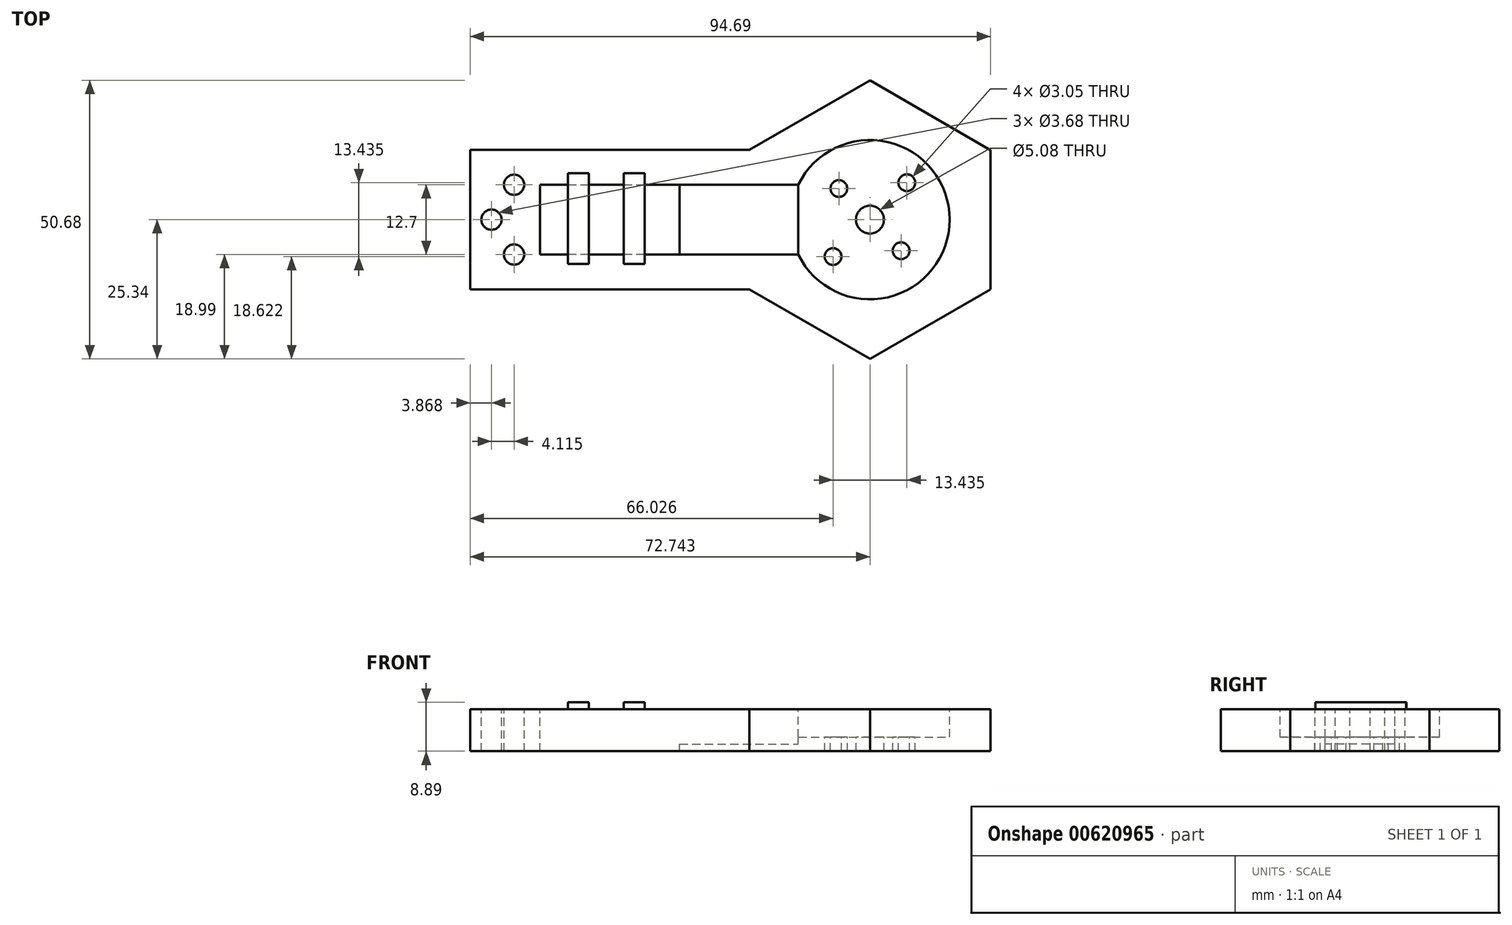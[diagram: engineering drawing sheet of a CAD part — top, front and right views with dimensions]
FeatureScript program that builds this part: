
annotation { "Feature Type Name" : "Feature", "Feature Type Description" : "" }
export const myFeature = defineFeature(function(context is Context, id is Id, definition is map)
    precondition{}
    {
        {
            var Q0;
            Q0=qCreatedBy(makeId("Top.planeOp"),FACE);
            var sketch = newSketch(context, id + "F0", { "sketchPlane" : qUnion([Q0])});
            skLineSegment(sketch, "E0.bottom", {"start": v(50.8, -12.7) * mm, "end": v(0, -12.7) * mm});
            skLineSegment(sketch, "E0.top", {"start": v(50.8, 12.7) * mm, "end": v(0, 12.7) * mm});
            skLineSegment(sketch, "E0.left", {"start": v(50.8, -12.7) * mm, "end": v(50.8, 12.7) * mm});
            skPoint(sketch, "E0.middle", {"position": v(0, 0) * mm});
            skLineSegment(sketch, "E1", {"start": v(0, 12.7) * mm, "end": v(0, -12.7) * mm});
            skPoint(sketch, "E2.orphan", {"position": v(-50.8, 12.7) * mm});
            skPoint(sketch, "E3.orphan", {"position": v(-50.8, -12.7) * mm});
            skSolve(sketch);
        }
        {
            var Q0;
            Q0=makeQuery(id+"F0.imprint","IMPRINT",FACE,{"disambiguationData":[TD([[makeQuery(id+"F0.imprint","IMPRINT",EDGE,{"derivedFrom":sQuery(id+"F0.wireOp",EDGE,"E0.bottom")}),-1.0]])]});
            extrude(context, id + "F1", {"entities" : qUnion([Q0]), "depth" : 7.62 * mm, "offsetDistance" : 25.4 * mm});
        }
        {
            var Q0;
            Q0=qCreatedBy(makeId("Top.planeOp"),FACE);
            var sketch = newSketch(context, id + "F2", { "sketchPlane" : qUnion([Q0])});
            skCircle(sketch, "E4.cCircle", {"center": v(72.74, 0) * mm, "radius": 21.95 * mm, "construction": true});
            skLineSegment(sketch, "E4.0", {"start": v(94.7, 12.67) * mm, "end": v(94.7, -12.67) * mm});
            skLineSegment(sketch, "E4.1", {"start": v(94.7, -12.67) * mm, "end": v(72.74, -25.34) * mm});
            skLineSegment(sketch, "E4.2", {"start": v(72.74, -25.34) * mm, "end": v(50.8, -12.67) * mm});
            skLineSegment(sketch, "E4.3", {"start": v(50.8, -12.67) * mm, "end": v(50.8, 12.67) * mm});
            skLineSegment(sketch, "E4.4", {"start": v(50.8, 12.67) * mm, "end": v(72.74, 25.34) * mm});
            skLineSegment(sketch, "E4.5", {"start": v(72.74, 25.34) * mm, "end": v(94.7, 12.67) * mm});
            skPoint(sketch, "E4.0.midPoint", {"position": v(94.7, 0) * mm});
            skSolve(sketch);
        }
        {
            var Q0;
            Q0=makeQuery(id+"F2.imprint","IMPRINT",FACE,{"disambiguationData":[TD([[makeQuery(id+"F2.imprint","IMPRINT",EDGE,{"derivedFrom":sQuery(id+"F2.wireOp",EDGE,"E4.0")}),-1.0]])]});
            extrude(context, id + "F3", {"entities" : qUnion([Q0]), "depth" : 7.62 * mm, "offsetDistance" : 25.4 * mm});
        }
        {
            var Q0;
            Q0=makeQuery(id+"F1.opExtrude","CAP_FACE",FACE,{"disambiguationData":[OSD([sQuery(id+"F0.wireOp",EDGE,"E0.bottom"),sQuery(id+"F0.wireOp",EDGE,"E0.top"),sQuery(id+"F0.wireOp",EDGE,"E0.left"),sQuery(id+"F0.wireOp",EDGE,"E0.right")])],"isStart":false});
            var sketch = newSketch(context, id + "F4", { "sketchPlane" : qUnion([Q0])});
            skLineSegment(sketch, "E5", {"start": v(12.7, 6.35) * mm, "end": v(38.1, 6.35) * mm});
            skLineSegment(sketch, "E6", {"start": v(38.1, 6.35) * mm, "end": v(38.1, -6.35) * mm});
            skLineSegment(sketch, "E7", {"start": v(38.1, -6.35) * mm, "end": v(12.7, -6.35) * mm});
            skLineSegment(sketch, "E8", {"start": v(12.7, -6.35) * mm, "end": v(12.7, 6.35) * mm});
            skSolve(sketch);
        }
        {
            var Q0;
            Q0=makeQuery(id+"F4.imprint","IMPRINT",FACE,{"disambiguationData":[TD([[makeQuery(id+"F4.imprint","IMPRINT",EDGE,{"derivedFrom":sQuery(id+"F4.wireOp",EDGE,"E5")}),-1.0]])]});
            extrude(context, id + "F5", {"entities" : qUnion([Q0]), "operationType" : NewBodyOperationType.REMOVE, "endBound" : BoundingType.THROUGH_ALL, "oppositeDirection" : true, "depth" : 25.4 * mm, "offsetDistance" : 25.4 * mm});
        }
        {
            var Q0;
            Q0=makeQuery(id+"F3.opExtrude","CAP_FACE",FACE,{"disambiguationData":[OSD([sQuery(id+"F2.wireOp",EDGE,"E4.0"),sQuery(id+"F2.wireOp",EDGE,"E4.1"),sQuery(id+"F2.wireOp",EDGE,"E4.2"),sQuery(id+"F2.wireOp",EDGE,"E4.3"),sQuery(id+"F2.wireOp",EDGE,"E4.4"),sQuery(id+"F2.wireOp",EDGE,"E4.5")])],"isStart":false});
            var sketch = newSketch(context, id + "F6", { "sketchPlane" : qUnion([Q0])});
            skCircle(sketch, "E9", {"center": v(72.74, 0) * mm, "radius": 14.5 * mm});
            skSolve(sketch);
        }
        {
            var Q0;
            Q0=qSketchRegion(id+"F6",true);
            extrude(context, id + "F7", {"entities" : qUnion([Q0]), "operationType" : NewBodyOperationType.REMOVE, "oppositeDirection" : true, "depth" : 5.08 * mm, "offsetDistance" : 25.4 * mm});
        }
        {
            var Q0;
            Q0=makeQuery(id+"F7.boolean.opBoolean","COPY",FACE,{"derivedFrom":makeQuery(id+"F7.opExtrude","CAP_FACE",FACE,{"disambiguationData":[OSD([sQuery(id+"F6.wireOp",EDGE,"E9")])],"isStart":false})});
            var sketch = newSketch(context, id + "F8", { "sketchPlane" : qUnion([Q0])});
            skLineSegment(sketch, "E10", {"start": v(72.74, 0) * mm, "end": v(79.46, 6.72) * mm});
            skSolve(sketch);
        }
        {
            var Q0;
            Q0=makeQuery(id+"F8.imprint","IMPRINT",FACE,{"disambiguationData":[TD([[makeQuery(id+"F8.imprint","IMPRINT",EDGE,{"derivedFrom":makeQuery(id+"F7.boolean.opBoolean","COPY",EDGE,{"derivedFrom":makeQuery(id+"F7.opExtrude","CAP_EDGE",EDGE,{"disambiguationData":[OSD([sQuery(id+"F6.wireOp",EDGE,"E9")])],"isStart":false})})}),1.0]])]});
            var sketch = newSketch(context, id + "F9", { "sketchPlane" : qUnion([Q0])});
            skCircle(sketch, "E11", {"center": v(67.09, 5.66) * mm, "radius": 1.52 * mm});
            skSolve(sketch);
        }
        {
            var Q0;
            Q0=makeQuery(id+"F8.imprint","IMPRINT",FACE,{"disambiguationData":[TD([[makeQuery(id+"F8.imprint","IMPRINT",EDGE,{"derivedFrom":makeQuery(id+"F7.boolean.opBoolean","COPY",EDGE,{"derivedFrom":makeQuery(id+"F7.opExtrude","CAP_EDGE",EDGE,{"disambiguationData":[OSD([sQuery(id+"F6.wireOp",EDGE,"E9")])],"isStart":false})})}),1.0]])]});
            var sketch = newSketch(context, id + "F10", { "sketchPlane" : qUnion([Q0])});
            skCircle(sketch, "E12", {"center": v(79.46, 6.72) * mm, "radius": 1.52 * mm});
            skSolve(sketch);
        }
        {
            var Q0;
            Q0=makeQuery(id+"F8.imprint","IMPRINT",FACE,{"disambiguationData":[TD([[makeQuery(id+"F8.imprint","IMPRINT",EDGE,{"derivedFrom":makeQuery(id+"F7.boolean.opBoolean","COPY",EDGE,{"derivedFrom":makeQuery(id+"F7.opExtrude","CAP_EDGE",EDGE,{"disambiguationData":[OSD([sQuery(id+"F6.wireOp",EDGE,"E9")])],"isStart":false})})}),1.0]])]});
            var sketch = newSketch(context, id + "F11", { "sketchPlane" : qUnion([Q0])});
            skCircle(sketch, "E13", {"center": v(78.4, -5.66) * mm, "radius": 1.52 * mm});
            skSolve(sketch);
        }
        {
            var Q0;
            Q0=makeQuery(id+"F8.imprint","IMPRINT",FACE,{"disambiguationData":[TD([[makeQuery(id+"F8.imprint","IMPRINT",EDGE,{"derivedFrom":makeQuery(id+"F7.boolean.opBoolean","COPY",EDGE,{"derivedFrom":makeQuery(id+"F7.opExtrude","CAP_EDGE",EDGE,{"disambiguationData":[OSD([sQuery(id+"F6.wireOp",EDGE,"E9")])],"isStart":false})})}),1.0]])]});
            var sketch = newSketch(context, id + "F12", { "sketchPlane" : qUnion([Q0])});
            skCircle(sketch, "E14", {"center": v(66.03, -6.72) * mm, "radius": 1.52 * mm});
            skSolve(sketch);
        }
        {
            var Q0;
            Q0=qSketchRegion(id+"F9",true);
            extrude(context, id + "F13", {"entities" : qUnion([Q0]), "operationType" : NewBodyOperationType.REMOVE, "endBound" : BoundingType.THROUGH_ALL, "oppositeDirection" : true, "depth" : 25.4 * mm, "offsetDistance" : 25.4 * mm});
        }
        {
            var Q0;
            Q0=qSketchRegion(id+"F10",true);
            extrude(context, id + "F14", {"entities" : qUnion([Q0]), "operationType" : NewBodyOperationType.REMOVE, "endBound" : BoundingType.THROUGH_ALL, "oppositeDirection" : true, "depth" : 25.4 * mm, "offsetDistance" : 25.4 * mm});
        }
        {
            var Q0;
            Q0=qSketchRegion(id+"F11",true);
            extrude(context, id + "F15", {"entities" : qUnion([Q0]), "operationType" : NewBodyOperationType.REMOVE, "endBound" : BoundingType.THROUGH_ALL, "oppositeDirection" : true, "depth" : 25.4 * mm, "offsetDistance" : 25.4 * mm});
        }
        {
            var Q0;
            Q0=qSketchRegion(id+"F12",true);
            extrude(context, id + "F16", {"entities" : qUnion([Q0]), "operationType" : NewBodyOperationType.REMOVE, "endBound" : BoundingType.THROUGH_ALL, "oppositeDirection" : true, "depth" : 25.4 * mm, "offsetDistance" : 25.4 * mm});
        }
        {
            var Q0;
            Q0=makeQuery(id+"F1.opExtrude","CAP_FACE",FACE,{"disambiguationData":[OSD([sQuery(id+"F0.wireOp",EDGE,"E0.bottom"),sQuery(id+"F0.wireOp",EDGE,"E0.top"),sQuery(id+"F0.wireOp",EDGE,"E0.left"),sQuery(id+"F0.wireOp",EDGE,"E0.right")])],"isStart":false});
            var sketch = newSketch(context, id + "F17", { "sketchPlane" : qUnion([Q0])});
            skLineSegment(sketch, "E15.bottom", {"start": v(17.78, -8.04) * mm, "end": v(21.59, -8.04) * mm});
            skLineSegment(sketch, "E15.top", {"start": v(17.78, 8.47) * mm, "end": v(21.59, 8.47) * mm});
            skLineSegment(sketch, "E15.left", {"start": v(17.78, -8.04) * mm, "end": v(17.78, 8.47) * mm});
            skLineSegment(sketch, "E15.right", {"start": v(21.59, -8.04) * mm, "end": v(21.59, 8.47) * mm});
            skLineSegment(sketch, "E16.bottom", {"start": v(27.94, -8.08) * mm, "end": v(31.75, -8.08) * mm});
            skLineSegment(sketch, "E16.top", {"start": v(27.94, 8.43) * mm, "end": v(31.75, 8.43) * mm});
            skLineSegment(sketch, "E16.left", {"start": v(27.94, -8.08) * mm, "end": v(27.94, 8.43) * mm});
            skLineSegment(sketch, "E16.right", {"start": v(31.75, -8.08) * mm, "end": v(31.75, 8.43) * mm});
            skSolve(sketch);
        }
        {
            var Q0;
            Q0=qSketchRegion(id+"F17",true);
            extrude(context, id + "F18", {"entities" : qUnion([Q0]), "operationType" : NewBodyOperationType.ADD, "depth" : 1.27 * mm, "offsetDistance" : 25.4 * mm});
        }
        {
            var Q0;
            Q0=makeQuery(id+"F1.opExtrude","CAP_FACE",FACE,{"disambiguationData":[OSD([sQuery(id+"F0.wireOp",EDGE,"E0.bottom"),sQuery(id+"F0.wireOp",EDGE,"E0.top"),sQuery(id+"F0.wireOp",EDGE,"E0.left"),sQuery(id+"F0.wireOp",EDGE,"E0.right")])],"isStart":false});
            var sketch = newSketch(context, id + "F19", { "sketchPlane" : qUnion([Q0])});
            skCircle(sketch, "E17", {"center": v(7.98, -6.35) * mm, "radius": 1.84 * mm});
            skCircle(sketch, "E18", {"center": v(7.98, 6.35) * mm, "radius": 1.84 * mm});
            skCircle(sketch, "E19", {"center": v(3.87, 0) * mm, "radius": 1.84 * mm});
            skSolve(sketch);
        }
        {
            var Q0;
            Q0=qSketchRegion(id+"F19",true);
            extrude(context, id + "F20", {"entities" : qUnion([Q0]), "operationType" : NewBodyOperationType.REMOVE, "endBound" : BoundingType.THROUGH_ALL, "oppositeDirection" : true, "depth" : 25.4 * mm, "offsetDistance" : 25.4 * mm});
        }
        {
            var Q0;
            Q0=makeQuery(id+"F1.opExtrude","SWEPT_BODY",BODY,{"disambiguationData":[OSD([sQuery(id+"F0.wireOp",EDGE,"E0.bottom"),sQuery(id+"F0.wireOp",EDGE,"E0.top"),sQuery(id+"F0.wireOp",EDGE,"E0.left"),sQuery(id+"F0.wireOp",EDGE,"E1")])]});
            var Q1;
            Q1=makeQuery(id+"F3.opExtrude","SWEPT_BODY",BODY,{"disambiguationData":[OSD([sQuery(id+"F2.wireOp",EDGE,"E4.0"),sQuery(id+"F2.wireOp",EDGE,"E4.1"),sQuery(id+"F2.wireOp",EDGE,"E4.2"),sQuery(id+"F2.wireOp",EDGE,"E4.3"),sQuery(id+"F2.wireOp",EDGE,"E4.4"),sQuery(id+"F2.wireOp",EDGE,"E4.5")])]});
            booleanBodies(context, id + "F21", {"operationType" : BooleanOperationType.UNION, "tools" : qUnion([Q0, Q1])});
        }
        {
            var Q0;
            Q0=makeQuery(id+"F21.opBoolean","MERGE",FACE,{"derivedFrom":[makeQuery(id+"F3.opExtrude","CAP_FACE",FACE,{"disambiguationData":[OSD([sQuery(id+"F2.wireOp",EDGE,"E4.0"),sQuery(id+"F2.wireOp",EDGE,"E4.1"),sQuery(id+"F2.wireOp",EDGE,"E4.2"),sQuery(id+"F2.wireOp",EDGE,"E4.3"),sQuery(id+"F2.wireOp",EDGE,"E4.4"),sQuery(id+"F2.wireOp",EDGE,"E4.5")])],"isStart":false}),makeQuery(id+"F1.opExtrude","CAP_FACE",FACE,{"disambiguationData":[OSD([sQuery(id+"F0.wireOp",EDGE,"E0.bottom"),sQuery(id+"F0.wireOp",EDGE,"E0.top"),sQuery(id+"F0.wireOp",EDGE,"E0.left"),sQuery(id+"F0.wireOp",EDGE,"E1")])],"isStart":false})]});
            var sketch = newSketch(context, id + "F22", { "sketchPlane" : qUnion([Q0])});
            skLineSegment(sketch, "E20.bottom", {"start": v(38.1, 6.35) * mm, "end": v(59.7, 6.35) * mm});
            skLineSegment(sketch, "E20.top", {"start": v(38.1, -6.35) * mm, "end": v(59.7, -6.35) * mm});
            skLineSegment(sketch, "E20.left", {"start": v(38.1, 6.35) * mm, "end": v(38.1, -6.35) * mm});
            skLineSegment(sketch, "E20.right", {"start": v(59.7, 6.35) * mm, "end": v(59.7, -6.35) * mm});
            skSolve(sketch);
        }
        {
            var Q0;
            Q0 = qSketchRegion(id + "F22", true);
            extrude(context, id + "F23", {"entities" : qUnion([Q0]), "operationType" : NewBodyOperationType.REMOVE, "oppositeDirection" : true, "depth" : 6.35 * mm, "offsetDistance" : 25.4 * mm});
        }
        {
            var Q0;
            Q0=makeQuery(id+"F7.boolean.opBoolean","COPY",FACE,{"derivedFrom":makeQuery(id+"F7.opExtrude","CAP_FACE",FACE,{"disambiguationData":[OSD([sQuery(id+"F6.wireOp",EDGE,"E9")])],"isStart":false})});
            var sketch = newSketch(context, id + "F24", { "sketchPlane" : qUnion([Q0])});
            skCircle(sketch, "E21", {"center": v(72.74, 0) * mm, "radius": 2.54 * mm});
            skSolve(sketch);
        }
        {
            var Q0;
            Q0 = qSketchRegion(id + "F24", true);
            extrude(context, id + "F25", {"entities" : qUnion([Q0]), "operationType" : NewBodyOperationType.REMOVE, "endBound" : BoundingType.THROUGH_ALL, "oppositeDirection" : true, "depth" : 25.4 * mm, "offsetDistance" : 25.4 * mm});
        }
    });
